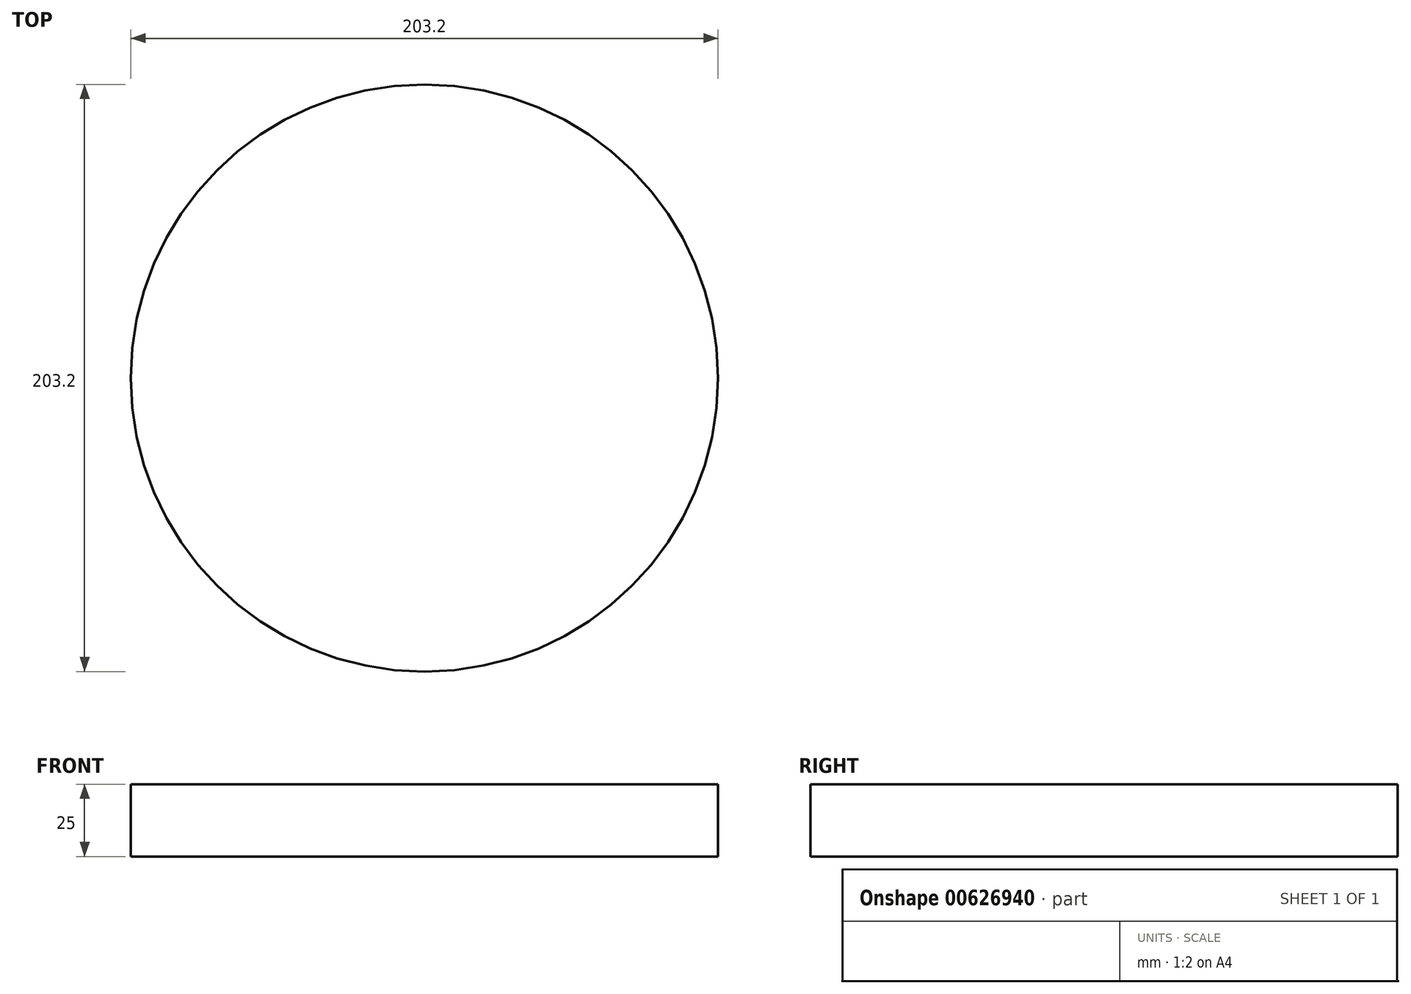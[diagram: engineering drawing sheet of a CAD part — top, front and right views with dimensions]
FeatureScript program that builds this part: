
annotation { "Feature Type Name" : "Feature", "Feature Type Description" : "" }
export const myFeature = defineFeature(function(context is Context, id is Id, definition is map)
    precondition{}
    {
        {
            var Q0;
            Q0=qCreatedBy(makeId("Top.planeOp"),FACE);
            var sketch = newSketch(context, id + "F0", { "sketchPlane" : qUnion([Q0])});
            skCircle(sketch, "E0", {"center": v(0, 0) * mm, "radius": 101.6 * mm});
            skSolve(sketch);
        }
        {
            var Q0;
            Q0=makeQuery(id+"F0.imprint","IMPRINT",FACE,{"disambiguationData":[TD([[makeQuery(id+"F0.imprint","IMPRINT",EDGE,{"derivedFrom":sQuery(id+"F0.wireOp",EDGE,"E0")}),1.0]])]});
            extrude(context, id + "F1", {"entities" : qUnion([Q0]), "depth" : 25 * mm, "offsetDistance" : 25 * mm});
        }
    });
